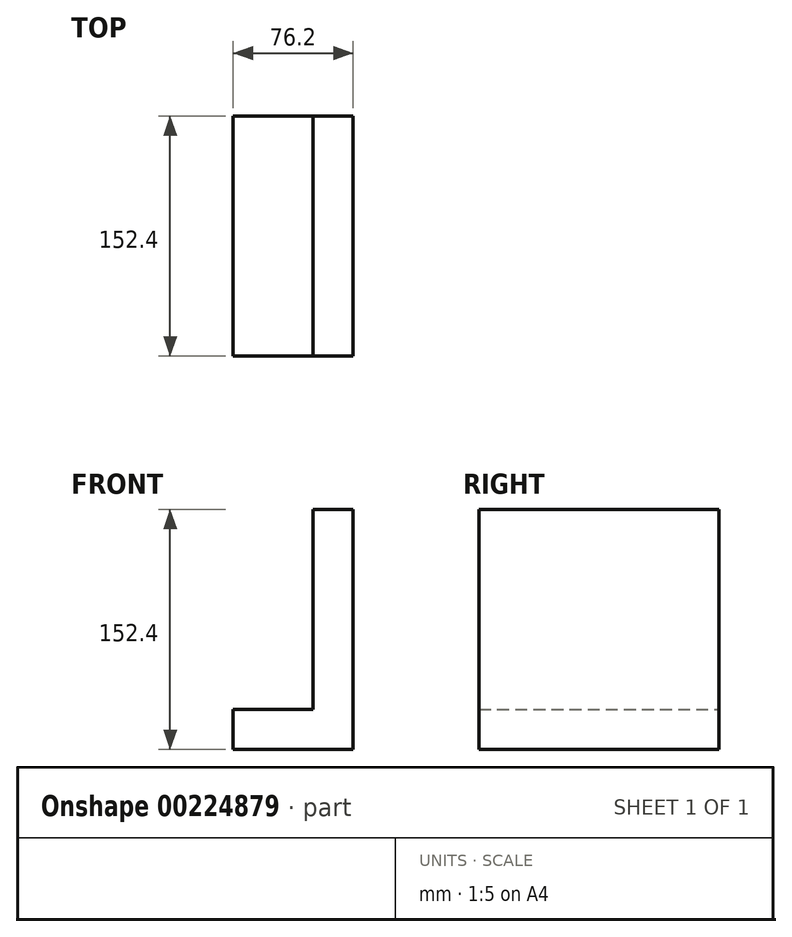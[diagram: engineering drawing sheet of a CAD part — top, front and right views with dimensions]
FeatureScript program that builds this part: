
annotation { "Feature Type Name" : "Feature", "Feature Type Description" : "" }
export const myFeature = defineFeature(function(context is Context, id is Id, definition is map)
    precondition{}
    {
        {
            var Q0;
            Q0=qCreatedBy(makeId("Front.planeOp"),FACE);
            var sketch = newSketch(context, id + "F0", { "sketchPlane" : qUnion([Q0])});
            skLineSegment(sketch, "E0", {"start": v(0, 0) * mm, "end": v(-76.2, 0) * mm});
            skLineSegment(sketch, "E1", {"start": v(-76.2, 0) * mm, "end": v(-76.2, 25.4) * mm});
            skLineSegment(sketch, "E2", {"start": v(-76.2, 25.4) * mm, "end": v(-25.4, 25.4) * mm});
            skLineSegment(sketch, "E3", {"start": v(-25.4, 25.4) * mm, "end": v(-25.4, 152.4) * mm});
            skLineSegment(sketch, "E4", {"start": v(-25.4, 152.4) * mm, "end": v(0, 152.4) * mm});
            skLineSegment(sketch, "E5", {"start": v(0, 152.4) * mm, "end": v(0, 0) * mm});
            skSolve(sketch);
        }
        {
            var Q0;
            Q0 = qSketchRegion(id + "F0", true);
            extrude(context, id + "F1", {"entities" : qUnion([Q0]), "endBound" : BoundingType.SYMMETRIC, "depth" : 152.4 * mm});
        }
    });
